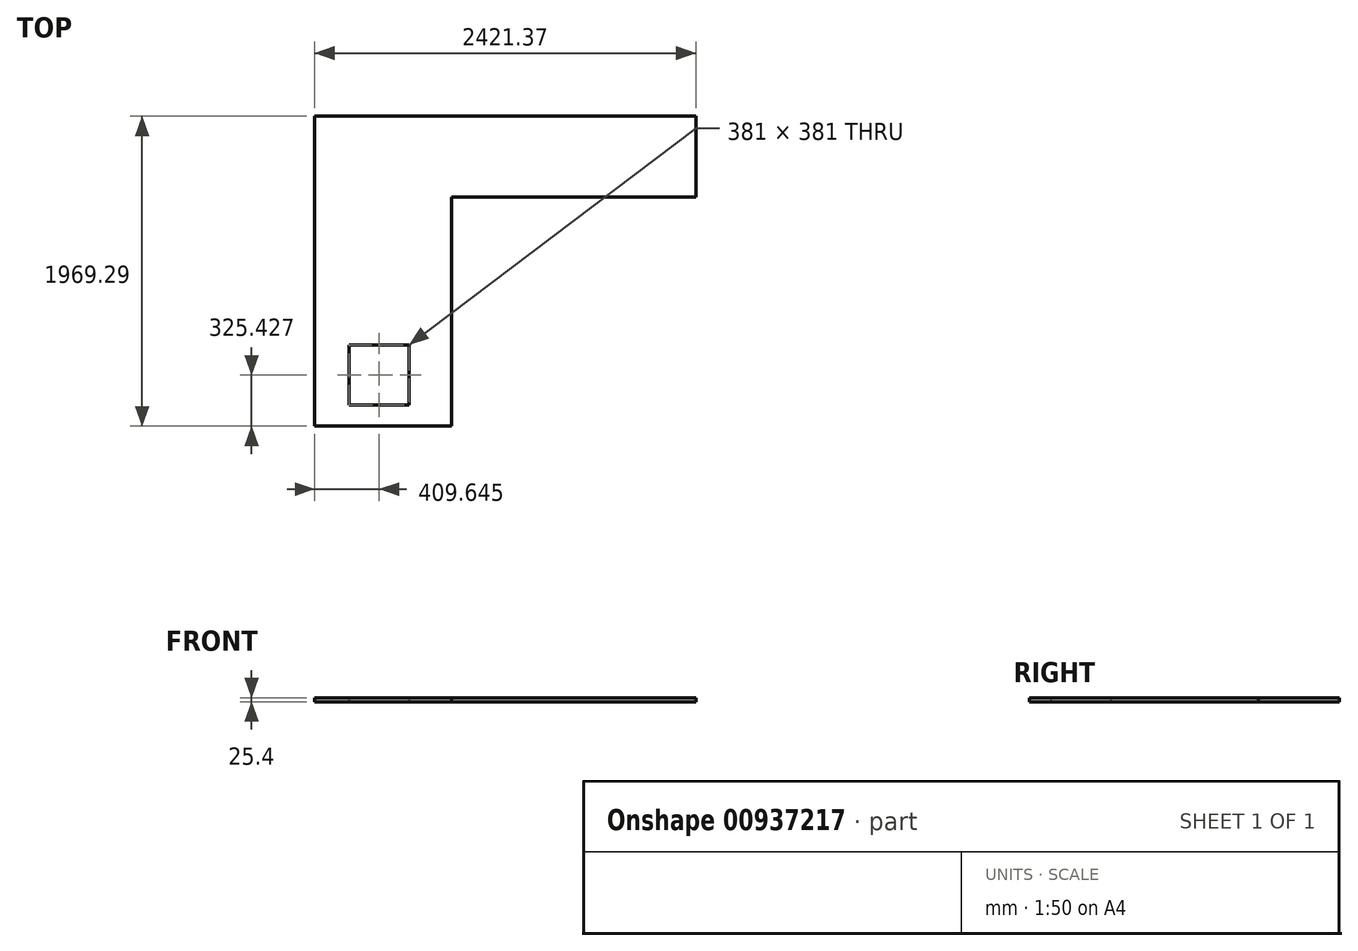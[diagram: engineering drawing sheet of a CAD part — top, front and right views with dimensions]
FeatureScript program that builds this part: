
annotation { "Feature Type Name" : "Feature", "Feature Type Description" : "" }
export const myFeature = defineFeature(function(context is Context, id is Id, definition is map)
    precondition{}
    {
        {
            var Q0;
            Q0=qCreatedBy(makeId("Top.planeOp"),FACE);
            var sketch = newSketch(context, id + "F0", { "sketchPlane" : qUnion([Q0])});
            skLineSegment(sketch, "E0.bottom", {"start": v(-432.06, -300.26) * mm, "end": v(-51.06, -300.26) * mm});
            skLineSegment(sketch, "E0.top", {"start": v(-432.06, -681.26) * mm, "end": v(-51.06, -681.26) * mm});
            skLineSegment(sketch, "E0.left", {"start": v(-432.06, -300.26) * mm, "end": v(-432.06, -681.26) * mm});
            skLineSegment(sketch, "E0.right", {"start": v(-51.06, -300.26) * mm, "end": v(-51.06, -681.26) * mm});
            skSolve(sketch);
        }
        {
            var Q0;
            Q0=makeQuery(id+"F0.imprint","IMPRINT",FACE,{"disambiguationData":[TD([[makeQuery(id+"F0.imprint","IMPRINT",EDGE,{"derivedFrom":sQuery(id+"F0.wireOp",EDGE,"E0.bottom")}),-1.0]])]});
            var sketch = newSketch(context, id + "F1", { "sketchPlane" : qUnion([Q0])});
            skLineSegment(sketch, "E1", {"start": v(-651.2, -816.2) * mm, "end": v(218.54, -816.2) * mm});
            skLineSegment(sketch, "E2", {"start": v(218.54, -816.2) * mm, "end": v(218.54, 638.02) * mm});
            skLineSegment(sketch, "E3", {"start": v(218.54, 638.02) * mm, "end": v(1770.16, 638.02) * mm});
            skLineSegment(sketch, "E4", {"start": v(1770.16, 638.02) * mm, "end": v(1770.16, 1153.1) * mm});
            skLineSegment(sketch, "E5", {"start": v(1770.16, 1153.1) * mm, "end": v(-651.2, 1153.1) * mm});
            skLineSegment(sketch, "E6", {"start": v(-651.2, 1153.1) * mm, "end": v(-651.2, -816.2) * mm});
            skSolve(sketch);
        }
        {
            var Q0;
            Q0=makeQuery(id+"F1.imprint","IMPRINT",FACE,{"disambiguationData":[TD([[makeQuery(id+"F1.imprint","IMPRINT",EDGE,{"derivedFrom":sQuery(id+"F1.wireOp",EDGE,"E1")}),1.0]])]});
            extrude(context, id + "F2", {"entities" : qUnion([Q0]), "depth" : 25.4 * mm, "offsetDistance" : 25.4 * mm});
        }
    });
